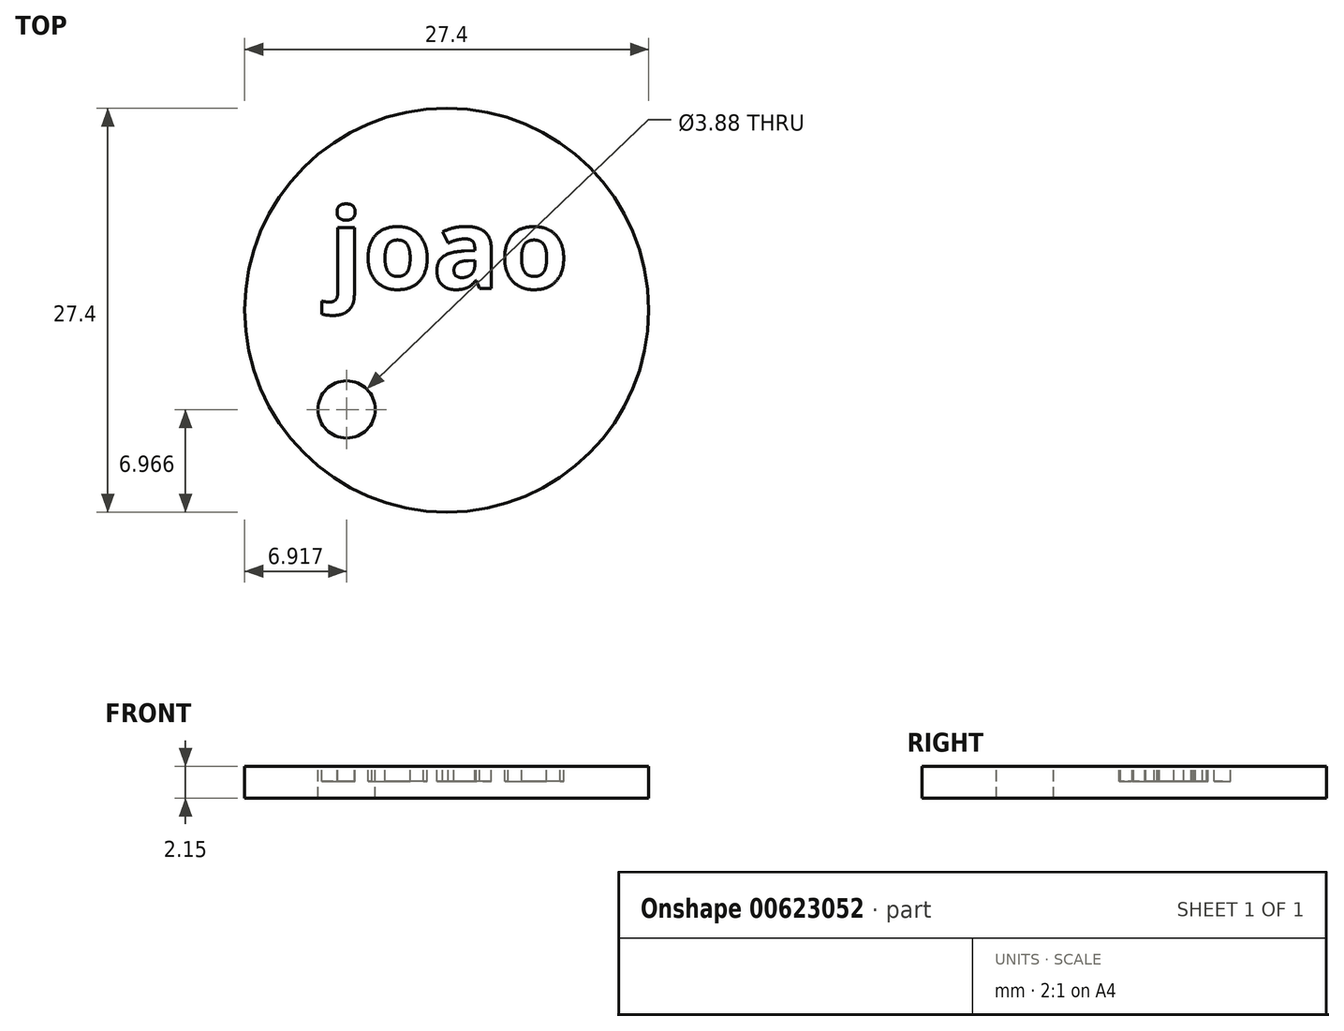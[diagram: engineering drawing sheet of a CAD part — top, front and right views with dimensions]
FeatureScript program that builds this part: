
annotation { "Feature Type Name" : "Feature", "Feature Type Description" : "" }
export const myFeature = defineFeature(function(context is Context, id is Id, definition is map)
    precondition{}
    {
        {
            var Q0;
            Q0=qCreatedBy(makeId("Top.planeOp"),FACE);
            var sketch = newSketch(context, id + "F0", { "sketchPlane" : qUnion([Q0])});
            skCircle(sketch, "E0", {"center": v(0, 0) * mm, "radius": 13.7 * mm});
            skSolve(sketch);
        }
        {
            var Q0;
            Q0=makeQuery(id+"F0.imprint","IMPRINT",FACE,{"disambiguationData":[TD([[makeQuery(id+"F0.imprint","IMPRINT",EDGE,{"derivedFrom":sQuery(id+"F0.wireOp",EDGE,"E0")}),1.0]])]});
            extrude(context, id + "F1", {"entities" : qUnion([Q0]), "depth" : 2.15 * mm, "offsetDistance" : 25 * mm});
        }
        {
            var Q0;
            Q0=makeQuery(id+"F1.opExtrude","CAP_FACE",FACE,{"disambiguationData":[OSD([sQuery(id+"F0.wireOp",EDGE,"E0")])],"isStart":false});
            var sketch = newSketch(context, id + "F2", { "sketchPlane" : qUnion([Q0])});
            skText(sketch, "E1", { "text": "joao", "fontName": "OpenSans-Bold.ttf"});
            skCircle(sketch, "E2", {"center": v(-6.78, -6.73) * mm, "radius": 1.94 * mm});
            const initialGuessF2  = {"E1": [-0.00798, 0.00146, 1, 0, 0.00545]};
            skSetInitialGuess(sketch, initialGuessF2);
            skSolve(sketch);
        }
        {
            var Q0;
            Q0 = qSketchRegion(id + "F2", true);
            extrude(context, id + "F3", {"entities" : qUnion([Q0]), "operationType" : NewBodyOperationType.REMOVE, "oppositeDirection" : true, "depth" : 1 * mm, "offsetDistance" : 25 * mm});
        }
        {
            var Q0;
            Q0=makeQuery(id+"F2.imprint","IMPRINT",FACE,{"disambiguationData":[TD([[makeQuery(id+"F2.imprint","IMPRINT",EDGE,{"derivedFrom":sQuery(id+"F2.wireOp",EDGE,"E2")}),1.0]])]});
            extrude(context, id + "F4", {"entities" : qUnion([Q0]), "operationType" : NewBodyOperationType.REMOVE, "endBound" : BoundingType.SYMMETRIC, "oppositeDirection" : true, "depth" : 25 * mm, "offsetDistance" : 25 * mm});
        }
    });
